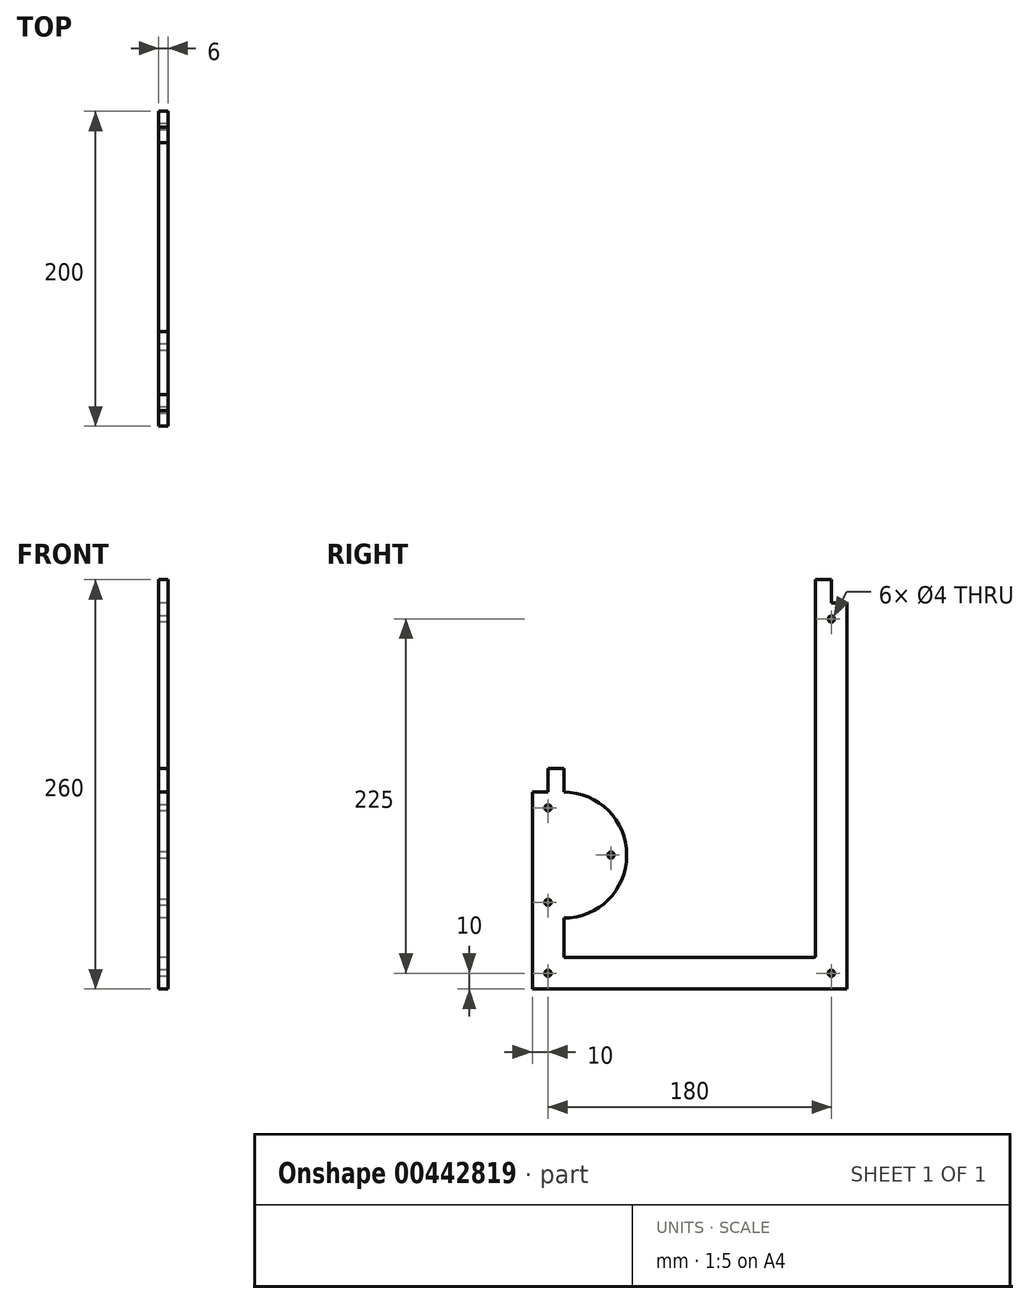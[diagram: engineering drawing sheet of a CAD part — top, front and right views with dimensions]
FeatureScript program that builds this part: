
annotation { "Feature Type Name" : "Feature", "Feature Type Description" : "" }
export const myFeature = defineFeature(function(context is Context, id is Id, definition is map)
    precondition{}
    {
        {
            var Q0;
            Q0=qCreatedBy(makeId("Right.planeOp"),FACE);
            var sketch = newSketch(context, id + "F0", { "sketchPlane" : qUnion([Q0])});
            skLineSegment(sketch, "E0.bottom", {"start": v(-1.27, 0) * mm, "end": v(-160, 0) * mm});
            skLineSegment(sketch, "E0.left", {"start": v(0, 1.27) * mm, "end": v(0, 240) * mm});
            skLineSegment(sketch, "E1.trimOffspring", {"start": v(-160, 105) * mm, "end": v(-160, 120) * mm});
            skPoint(sketch, "E2.visualSharp", {"position": v(0, 0) * mm});
            skArc(sketch, "E2.filletArc", {"start": v(-1.27, 0) * mm, "mid": v(-0.37, 0.37) * mm, "end": v(0, 1.27) * mm});
            skLineSegment(sketch, "E3", {"start": v(-160, 0) * mm, "end": v(-160, 25) * mm});
            skArc(sketch, "E4", {"start": v(-160, 25) * mm, "mid": v(-120, 65) * mm, "end": v(-160, 105) * mm});
            skLineSegment(sketch, "E5", {"start": v(-170, 105) * mm, "end": v(-180, 105) * mm});
            skLineSegment(sketch, "E6", {"start": v(-170, 105) * mm, "end": v(-170, 120) * mm});
            skLineSegment(sketch, "E7", {"start": v(-170, 120) * mm, "end": v(-160, 120) * mm});
            skLineSegment(sketch, "E8", {"start": v(-160, 105) * mm, "end": v(-160, -34) * mm, "construction": true});
            skLineSegment(sketch, "E9", {"start": v(20, 225) * mm, "end": v(10, 225) * mm});
            skLineSegment(sketch, "E10", {"start": v(10, 225) * mm, "end": v(10, 240) * mm});
            skLineSegment(sketch, "E11", {"start": v(10, 240) * mm, "end": v(0, 240) * mm});
            skLineSegment(sketch, "E12", {"start": v(-180, 105) * mm, "end": v(-180, -20) * mm});
            skLineSegment(sketch, "E13", {"start": v(20, 225) * mm, "end": v(20, -20) * mm});
            skLineSegment(sketch, "E14", {"start": v(20, -20) * mm, "end": v(-180, -20) * mm});
            skCircle(sketch, "E15", {"center": v(-170, 95) * mm, "radius": 2 * mm});
            skCircle(sketch, "E16", {"center": v(-170, 35) * mm, "radius": 2 * mm});
            skCircle(sketch, "E17", {"center": v(-170, -10) * mm, "radius": 2 * mm});
            skCircle(sketch, "E18", {"center": v(10, -10) * mm, "radius": 2 * mm});
            skCircle(sketch, "E19", {"center": v(10, 215) * mm, "radius": 2 * mm});
            skCircle(sketch, "E20", {"center": v(-130, 65) * mm, "radius": 2 * mm});
            skPoint(sketch, "E20.centerSnap0", {"position": v(-120, 65) * mm});
            skSolve(sketch);
        }
        {
            var Q0;
            Q0=qSketchRegion(id+"F0",true);
            extrude(context, id + "F1", {"entities" : qUnion([Q0]), "depth" : 6 * mm, "offsetDistance" : 25 * mm});
        }
    });
